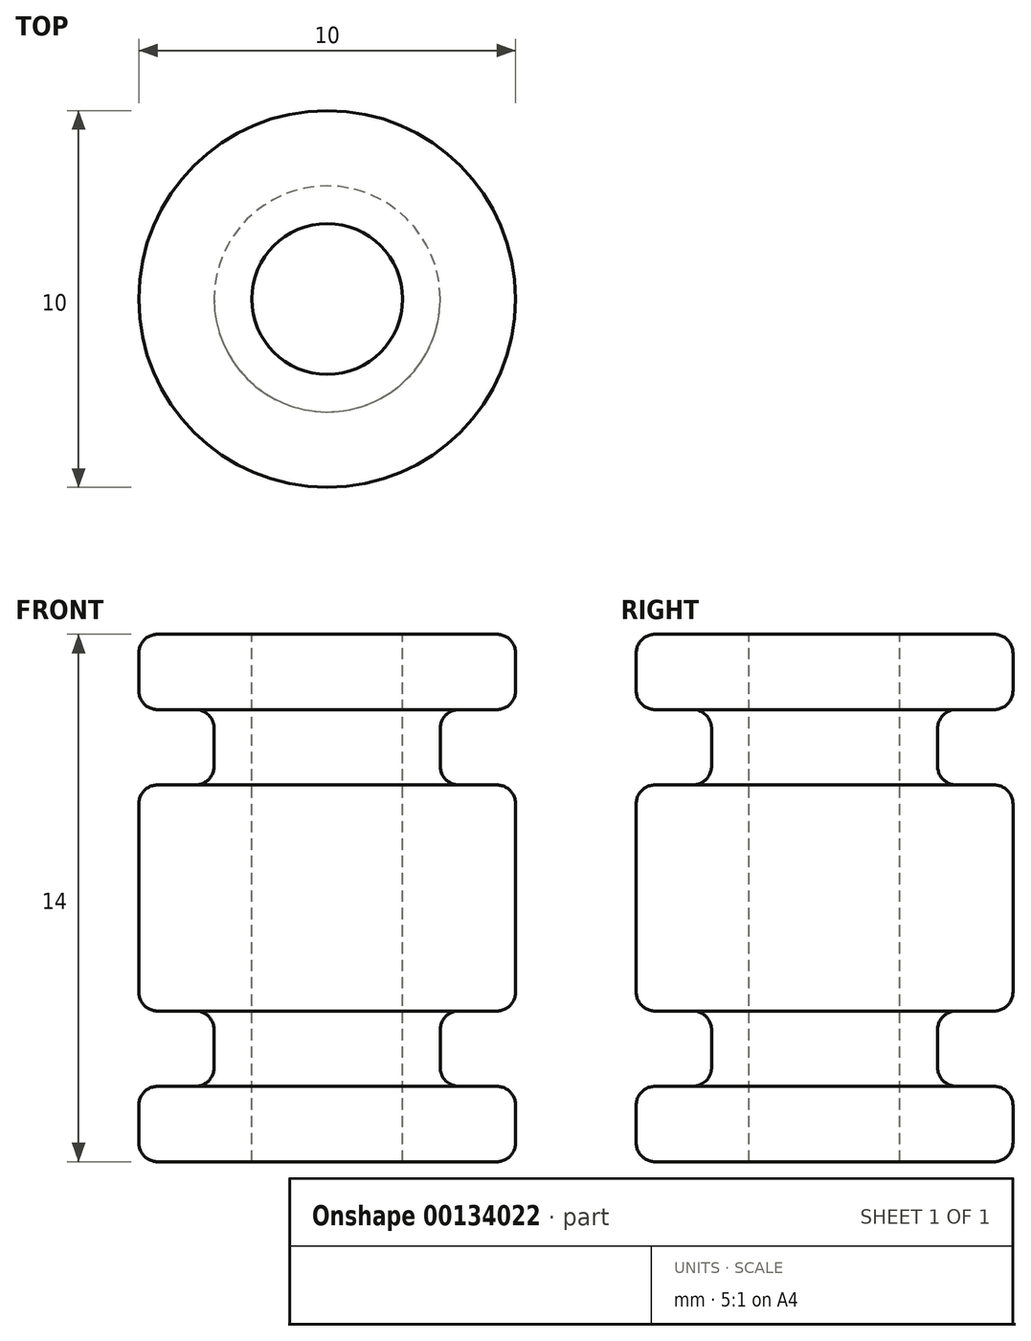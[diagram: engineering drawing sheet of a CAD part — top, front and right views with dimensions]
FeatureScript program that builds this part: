
annotation { "Feature Type Name" : "Feature", "Feature Type Description" : "" }
export const myFeature = defineFeature(function(context is Context, id is Id, definition is map)
    precondition{}
    {
        {
            var Q0;
            Q0=qCreatedBy(makeId("Front.planeOp"),FACE);
            var sketch = newSketch(context, id + "F0", { "sketchPlane" : qUnion([Q0])});
            skLineSegment(sketch, "E0", {"start": v(0, 7) * mm, "end": v(-5, 7) * mm});
            skLineSegment(sketch, "E1", {"start": v(-5, 7) * mm, "end": v(-5, 5) * mm});
            skLineSegment(sketch, "E2", {"start": v(-5, 5) * mm, "end": v(-3, 5) * mm});
            skLineSegment(sketch, "E3", {"start": v(-3, 5) * mm, "end": v(-3, 3) * mm});
            skLineSegment(sketch, "E4", {"start": v(-3, 3) * mm, "end": v(-5, 3) * mm});
            skLineSegment(sketch, "E5", {"start": v(-5, 3) * mm, "end": v(-5, -3) * mm});
            skLineSegment(sketch, "E6", {"start": v(-5, -3) * mm, "end": v(-3, -3) * mm});
            skLineSegment(sketch, "E7", {"start": v(-3, -3) * mm, "end": v(-3, -5) * mm});
            skLineSegment(sketch, "E8", {"start": v(-3, -5) * mm, "end": v(-5, -5) * mm});
            skLineSegment(sketch, "E9", {"start": v(-5, -5) * mm, "end": v(-5, -7) * mm});
            skLineSegment(sketch, "E10", {"start": v(-5, -7) * mm, "end": v(0, -7) * mm});
            skLineSegment(sketch, "E11", {"start": v(0, -7) * mm, "end": v(0, 7) * mm});
            skSolve(sketch);
        }
        {
            var Q0;
            Q0=makeQuery(id+"F0.imprint","IMPRINT",FACE,{"disambiguationData":[TD([[makeQuery(id+"F0.imprint","IMPRINT",EDGE,{"derivedFrom":sQuery(id+"F0.wireOp",EDGE,"E0")}),1.0]])]});
            var Q1;
            Q1=sQuery(id+"F0.wireOp",EDGE,"E11");
            revolve(context, id + "F1", {"surfaceOperationType" : NewSurfaceOperationType.NEW, "entities" : qUnion([Q0]), "axis" : qUnion([Q1]), "revolveType" : RevolveType.FULL});
        }
        {
            var Q0;
            Q0=qCreatedBy(makeId("Top.planeOp"),FACE);
            var sketch = newSketch(context, id + "F2", { "sketchPlane" : qUnion([Q0])});
            skCircle(sketch, "E12", {"center": v(0, 0) * mm, "radius": 2 * mm});
            skSolve(sketch);
        }
        {
            var Q0;
            Q0 = qSketchRegion(id + "F2", true);
            extrude(context, id + "F3", {"entities" : qUnion([Q0]), "operationType" : NewBodyOperationType.REMOVE, "endBound" : BoundingType.SYMMETRIC, "oppositeDirection" : true, "depth" : 100 * mm, "offsetDistance" : 25 * mm});
        }
        {
            var Q0;
            Q0=makeQuery(id+"F1.opRevolve","SWEPT_FACE",FACE,{"disambiguationData":[OSD([sQuery(id+"F0.wireOp",EDGE,"E1")])]});
            var Q1;
            Q1=makeQuery(id+"F1.opRevolve","SWEPT_FACE",FACE,{"disambiguationData":[OSD([sQuery(id+"F0.wireOp",EDGE,"E5")])]});
            var Q2;
            Q2=makeQuery(id+"F1.opRevolve","SWEPT_FACE",FACE,{"disambiguationData":[OSD([sQuery(id+"F0.wireOp",EDGE,"E9")])]});
            var Q3;
            Q3=makeQuery(id+"F1.opRevolve","SWEPT_FACE",FACE,{"disambiguationData":[OSD([sQuery(id+"F0.wireOp",EDGE,"E7")])]});
            var Q4;
            Q4=makeQuery(id+"F1.opRevolve","SWEPT_FACE",FACE,{"disambiguationData":[OSD([sQuery(id+"F0.wireOp",EDGE,"E3")])]});
            fillet(context, id + "F4", {"entities" : qUnion([Q0, Q1, Q2, Q3, Q4]), "radius" : 0.5 * mm, "tangentPropagation" : true, "allowEdgeOverflow" : false});
        }
    });
